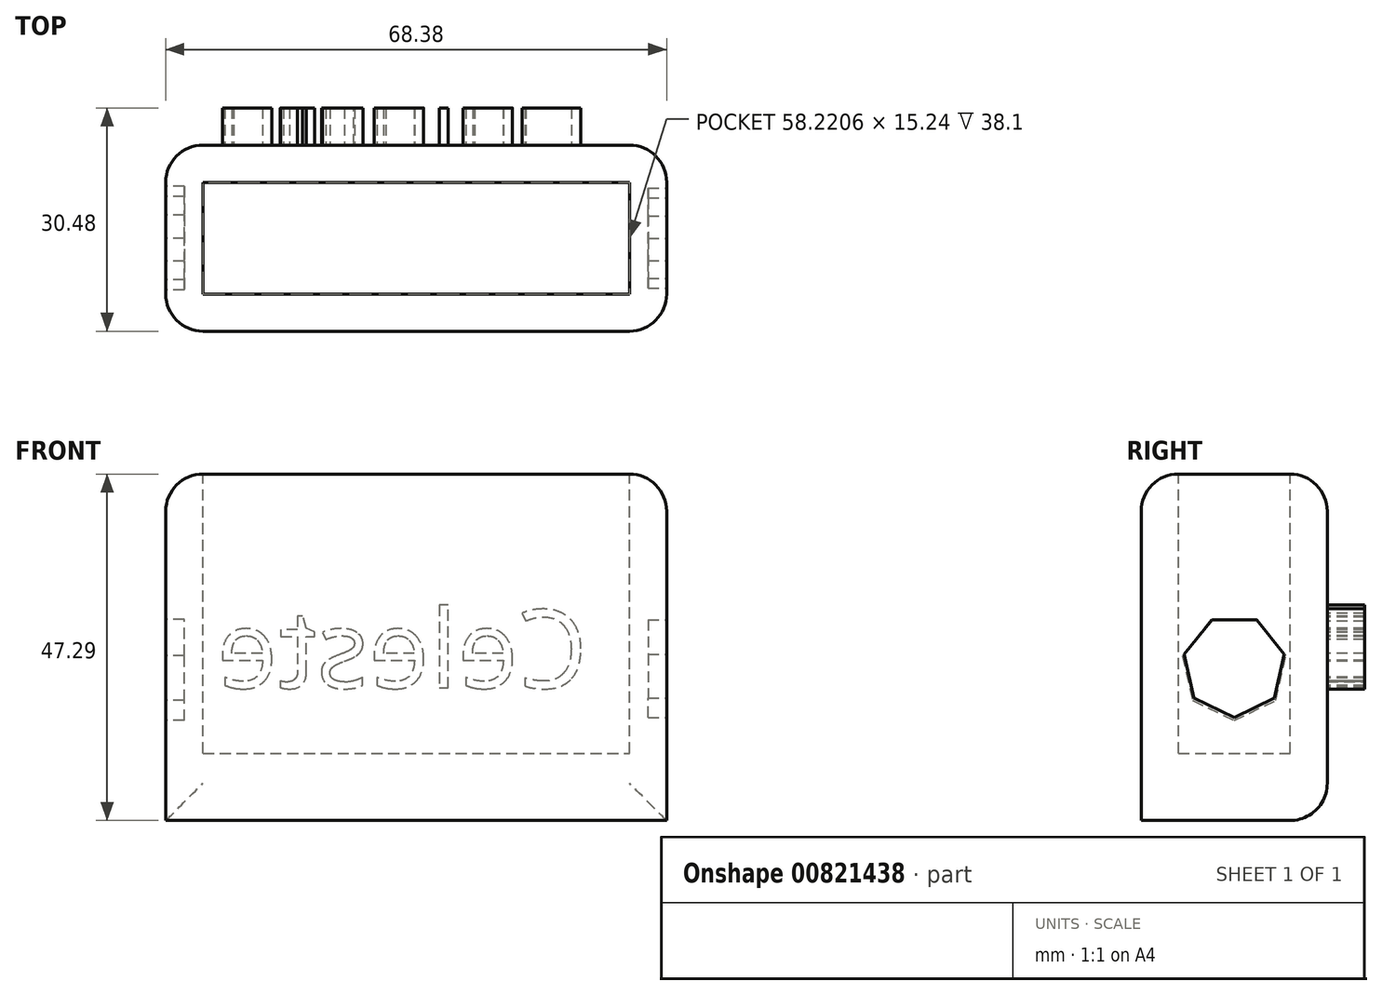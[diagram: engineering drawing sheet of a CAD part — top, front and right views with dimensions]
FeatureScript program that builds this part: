
annotation { "Feature Type Name" : "Feature", "Feature Type Description" : "" }
export const myFeature = defineFeature(function(context is Context, id is Id, definition is map)
    precondition{}
    {
        {
            var Q0;
            Q0=qCreatedBy(makeId("Front.planeOp"),FACE);
            var sketch = newSketch(context, id + "F0", { "sketchPlane" : qUnion([Q0])});
            skLineSegment(sketch, "E0.bottom", {"start": v(0, 0) * mm, "end": v(68.38, 0) * mm});
            skLineSegment(sketch, "E0.top", {"start": v(0, 47.3) * mm, "end": v(68.38, 47.3) * mm});
            skLineSegment(sketch, "E0.left", {"start": v(0, 0) * mm, "end": v(0, 47.3) * mm});
            skLineSegment(sketch, "E0.right", {"start": v(68.38, 0) * mm, "end": v(68.38, 47.3) * mm});
            skSolve(sketch);
        }
        {
            var Q0;
            Q0 = qSketchRegion(id + "F0", true);
            extrude(context, id + "F1", {"entities" : qUnion([Q0]), "depth" : 25.4 * mm, "offsetDistance" : 25.4 * mm});
        }
        {
            var Q0;
            Q0=makeQuery(id+"F1.opExtrude","CAP_EDGE",EDGE,{"disambiguationData":[OSD([sQuery(id+"F0.wireOp",EDGE,"E0.top")])],"isStart":false});
            var Q1;
            Q1=makeQuery(id+"F1.opExtrude","CAP_EDGE",EDGE,{"disambiguationData":[OSD([sQuery(id+"F0.wireOp",EDGE,"E0.right")])],"isStart":false});
            var Q2;
            Q2=makeQuery(id+"F1.opExtrude","SWEPT_EDGE",EDGE,{"disambiguationData":[OSD([sQuery(id+"F0.wireOp",EDGE,"E0.top"),sQuery(id+"F0.wireOp",EDGE,"E0.right")])]});
            var Q3;
            Q3=makeQuery(id+"F1.opExtrude","CAP_EDGE",EDGE,{"disambiguationData":[OSD([sQuery(id+"F0.wireOp",EDGE,"E0.right")])],"isStart":true});
            var Q4;
            Q4=makeQuery(id+"F1.opExtrude","CAP_EDGE",EDGE,{"disambiguationData":[OSD([sQuery(id+"F0.wireOp",EDGE,"E0.left")])],"isStart":false});
            var Q5;
            Q5=makeQuery(id+"F1.opExtrude","CAP_FACE",FACE,{"disambiguationData":[OSD([sQuery(id+"F0.wireOp",EDGE,"E0.bottom"),sQuery(id+"F0.wireOp",EDGE,"E0.top"),sQuery(id+"F0.wireOp",EDGE,"E0.left"),sQuery(id+"F0.wireOp",EDGE,"E0.right")])],"isStart":true});
            var Q6;
            Q6=makeQuery(id+"F1.opExtrude","CAP_EDGE",EDGE,{"disambiguationData":[OSD([sQuery(id+"F0.wireOp",EDGE,"E0.left")])],"isStart":true});
            var Q7;
            Q7=makeQuery(id+"F1.opExtrude","SWEPT_EDGE",EDGE,{"disambiguationData":[OSD([sQuery(id+"F0.wireOp",EDGE,"E0.top"),sQuery(id+"F0.wireOp",EDGE,"E0.left")])]});
            fillet(context, id + "F2", {"entities" : qUnion([Q0, Q1, Q2, Q3, Q4, Q5, Q6, Q7]), "radius" : 5.08 * mm, "tangentPropagation" : true, "allowEdgeOverflow" : false});
        }
        {
            var Q0;
            Q0=makeQuery(id+"F1.opExtrude","CAP_FACE",FACE,{"disambiguationData":[OSD([sQuery(id+"F0.wireOp",EDGE,"E0.bottom"),sQuery(id+"F0.wireOp",EDGE,"E0.top"),sQuery(id+"F0.wireOp",EDGE,"E0.left"),sQuery(id+"F0.wireOp",EDGE,"E0.right")])],"isStart":true});
            var sketch = newSketch(context, id + "F3", { "sketchPlane" : qUnion([Q0])});
            skText(sketch, "E1", { "text": "Celeste", "fontName": "OpenSans-Regular.ttf"});
            const initialGuessF3  = {"E1": [-0.05758, 0.0181, 1, 0, 0.01073]};
            skSetInitialGuess(sketch, initialGuessF3);
            skSolve(sketch);
        }
        {
            var Q0;
            Q0 = qSketchRegion(id + "F3", true);
            extrude(context, id + "F4", {"entities" : qUnion([Q0]), "operationType" : NewBodyOperationType.ADD, "depth" : 5.08 * mm, "offsetDistance" : 25.4 * mm});
        }
        {
            var Q0;
            Q0=makeQuery(id+"F1.opExtrude","SWEPT_FACE",FACE,{"disambiguationData":[OSD([sQuery(id+"F0.wireOp",EDGE,"E0.top")])]});
            var sketch = newSketch(context, id + "F5", { "sketchPlane" : qUnion([Q0])});
            skLineSegment(sketch, "E2.bottom", {"start": v(63.3, -20.32) * mm, "end": v(5.08, -20.32) * mm});
            skLineSegment(sketch, "E2.left", {"start": v(63.3, -20.32) * mm, "end": v(63.3, -5.8) * mm});
            skLineSegment(sketch, "E2.right", {"start": v(5.08, -20.32) * mm, "end": v(5.08, -5.8) * mm});
            skSolve(sketch);
        }
        {
            var Q0;
            Q0 = qSketchRegion(id + "F5", true);
            var Q1;
            Q1=makeQuery(id+"F5.imprint","IMPRINT",FACE,{"disambiguationData":[TD([[makeQuery(id+"F5.imprint","IMPRINT",EDGE,{"derivedFrom":sQuery(id+"F5.wireOp",EDGE,"E2.bottom")}),1.0]])]});
            extrude(context, id + "F6", {"entities" : qUnion([Q0, Q1]), "operationType" : NewBodyOperationType.REMOVE, "oppositeDirection" : true, "depth" : 38.1 * mm, "offsetDistance" : 25.4 * mm});
        }
        {
            var Q0;
            Q0=makeQuery(id+"F1.opExtrude","SWEPT_FACE",FACE,{"disambiguationData":[OSD([sQuery(id+"F0.wireOp",EDGE,"E0.left")])]});
            var sketch = newSketch(context, id + "F7", { "sketchPlane" : qUnion([Q0])});
            skLineSegment(sketch, "E3", {"start": v(12.7, 42.21) * mm, "end": v(12.7, 0) * mm});
            skCircle(sketch, "E4.cCircle", {"center": v(12.7, 20.9) * mm, "radius": 6.53 * mm, "construction": true});
            skLineSegment(sketch, "E4.0", {"start": v(9.56, 27.43) * mm, "end": v(15.84, 27.43) * mm});
            skLineSegment(sketch, "E4.1", {"start": v(15.84, 27.43) * mm, "end": v(19.76, 22.52) * mm});
            skLineSegment(sketch, "E4.2", {"start": v(19.76, 22.52) * mm, "end": v(18.36, 16.39) * mm});
            skLineSegment(sketch, "E4.3", {"start": v(18.36, 16.39) * mm, "end": v(12.7, 13.66) * mm});
            skLineSegment(sketch, "E4.4", {"start": v(12.7, 13.66) * mm, "end": v(7.04, 16.39) * mm});
            skLineSegment(sketch, "E4.5", {"start": v(7.04, 16.39) * mm, "end": v(5.64, 22.52) * mm});
            skLineSegment(sketch, "E4.6", {"start": v(5.64, 22.52) * mm, "end": v(9.56, 27.43) * mm});
            skPoint(sketch, "E4.0.midPoint", {"position": v(12.7, 27.43) * mm});
            skSolve(sketch);
        }
        {
            var Q0;
            {var subQ0=sQuery(id+"F7.wireOp",EDGE,"E4.1");Q0=makeQuery(id+"F7.imprint","IMPRINT",FACE,{"disambiguationData":[TD([[makeQuery(id+"F7.imprint","IMPRINT",EDGE,{"derivedFrom":subQ0}),-1.0]])]});}
            var Q1;
            {var subQ0=sQuery(id+"F7.wireOp",EDGE,"E4.4");Q1=makeQuery(id+"F7.imprint","IMPRINT",FACE,{"disambiguationData":[TD([[makeQuery(id+"F7.imprint","IMPRINT",EDGE,{"derivedFrom":subQ0}),-1.0]])]});}
            extrude(context, id + "F8", {"entities" : qUnion([Q0, Q1]), "operationType" : NewBodyOperationType.REMOVE, "oppositeDirection" : true, "depth" : 2.54 * mm, "offsetDistance" : 25.4 * mm});
        }
        {
            var Q0;
            Q0=makeQuery(id+"F1.opExtrude","SWEPT_FACE",FACE,{"disambiguationData":[OSD([sQuery(id+"F0.wireOp",EDGE,"E0.right")])]});
            var sketch = newSketch(context, id + "F9", { "sketchPlane" : qUnion([Q0])});
            skLineSegment(sketch, "E5", {"start": v(-12.7, 42.21) * mm, "end": v(-12.7, 0) * mm});
            skCircle(sketch, "E6.cCircle", {"center": v(-12.7, 21.1) * mm, "radius": 6.32 * mm, "construction": true});
            skLineSegment(sketch, "E6.0", {"start": v(-15.74, 27.43) * mm, "end": v(-9.66, 27.43) * mm});
            skLineSegment(sketch, "E6.1", {"start": v(-9.66, 27.43) * mm, "end": v(-5.86, 22.67) * mm});
            skLineSegment(sketch, "E6.2", {"start": v(-5.86, 22.67) * mm, "end": v(-7.22, 16.73) * mm});
            skLineSegment(sketch, "E6.3", {"start": v(-7.22, 16.73) * mm, "end": v(-12.7, 14.1) * mm});
            skLineSegment(sketch, "E6.4", {"start": v(-12.7, 14.1) * mm, "end": v(-18.18, 16.73) * mm});
            skLineSegment(sketch, "E6.5", {"start": v(-18.18, 16.73) * mm, "end": v(-19.54, 22.67) * mm});
            skLineSegment(sketch, "E6.6", {"start": v(-19.54, 22.67) * mm, "end": v(-15.74, 27.43) * mm});
            skPoint(sketch, "E6.0.midPoint", {"position": v(-12.7, 27.43) * mm});
            skSolve(sketch);
        }
        {
            var Q0;
            {var subQ0=sQuery(id+"F9.wireOp",EDGE,"E6.4");Q0=makeQuery(id+"F9.imprint","IMPRINT",FACE,{"disambiguationData":[TD([[makeQuery(id+"F9.imprint","IMPRINT",EDGE,{"derivedFrom":subQ0}),-1.0]])]});}
            var Q1;
            {var subQ0=sQuery(id+"F9.wireOp",EDGE,"E6.1");Q1=makeQuery(id+"F9.imprint","IMPRINT",FACE,{"disambiguationData":[TD([[makeQuery(id+"F9.imprint","IMPRINT",EDGE,{"derivedFrom":subQ0}),-1.0]])]});}
            extrude(context, id + "F10", {"entities" : qUnion([Q0, Q1]), "operationType" : NewBodyOperationType.REMOVE, "oppositeDirection" : true, "depth" : 2.54 * mm, "offsetDistance" : 25.4 * mm});
        }
    });
